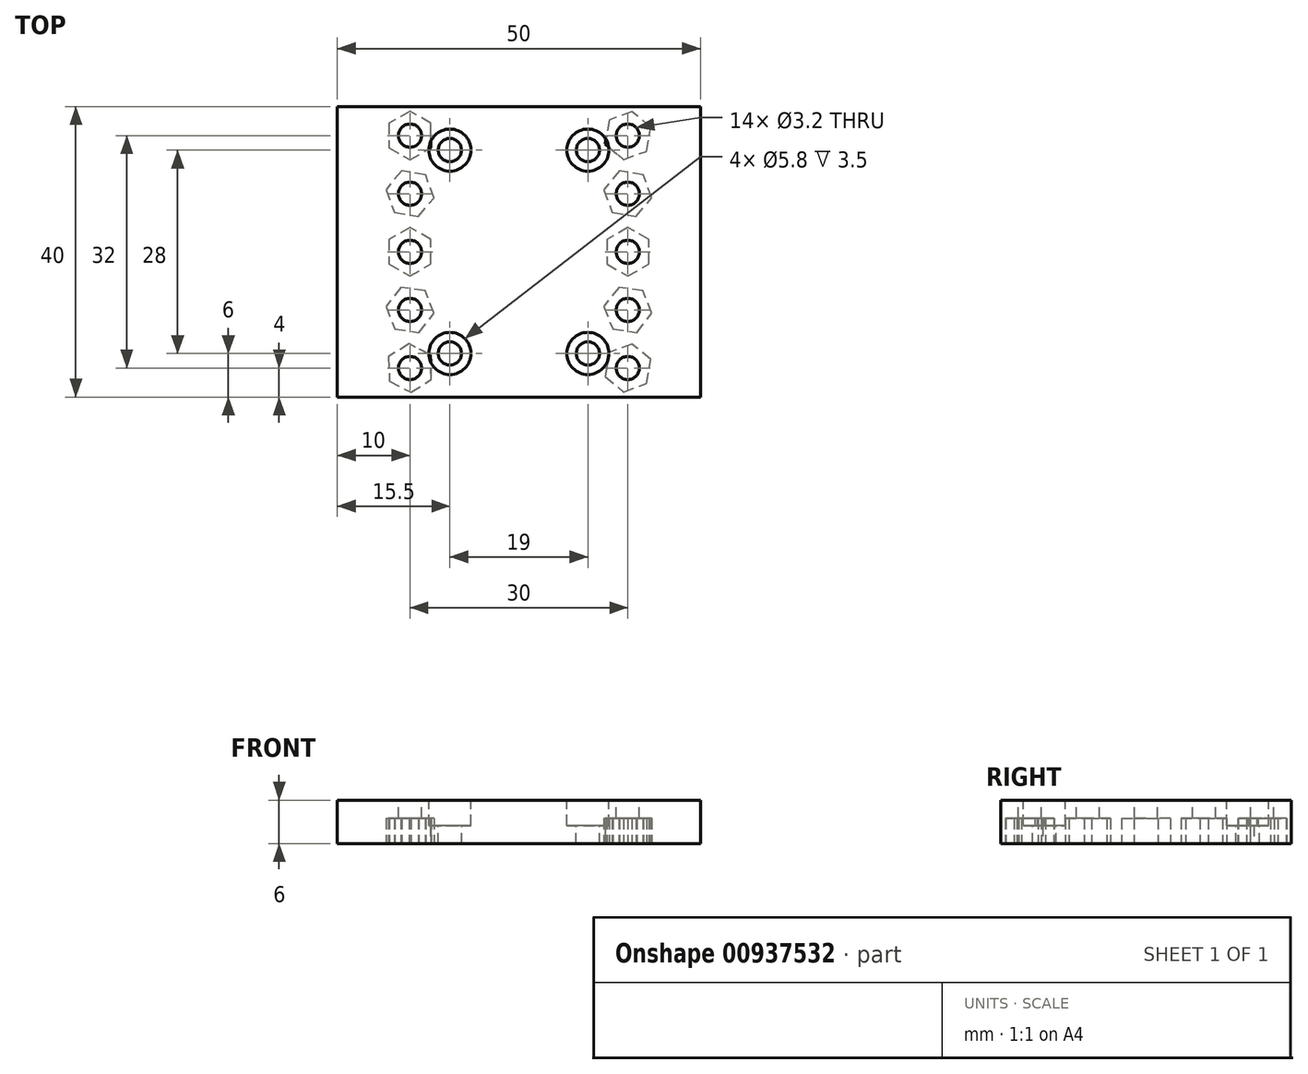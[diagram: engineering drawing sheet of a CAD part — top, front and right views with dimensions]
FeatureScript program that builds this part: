
annotation { "Feature Type Name" : "Feature", "Feature Type Description" : "" }
export const myFeature = defineFeature(function(context is Context, id is Id, definition is map)
    precondition{}
    {
        {
            var Q0;
            Q0=qCreatedBy(makeId("Top.planeOp"),FACE);
            var sketch = newSketch(context, id + "F0", { "sketchPlane" : qUnion([Q0])});
            skLineSegment(sketch, "E0.bottom", {"start": v(25, 20) * mm, "end": v(-25, 20) * mm});
            skLineSegment(sketch, "E0.top", {"start": v(25, -20) * mm, "end": v(-25, -20) * mm});
            skLineSegment(sketch, "E0.left", {"start": v(25, 20) * mm, "end": v(25, -20) * mm});
            skLineSegment(sketch, "E0.right", {"start": v(-25, 20) * mm, "end": v(-25, -20) * mm});
            skPoint(sketch, "E0.middle", {"position": v(0, 0) * mm});
            skSolve(sketch);
        }
        {
            var Q0;
            Q0=makeQuery(id+"F0.imprint","IMPRINT",FACE,{"disambiguationData":[TD([[makeQuery(id+"F0.imprint","IMPRINT",EDGE,{"derivedFrom":sQuery(id+"F0.wireOp",EDGE,"E0.bottom")}),1.0]])]});
            extrude(context, id + "F1", {"entities" : qUnion([Q0]), "depth" : 6 * mm, "offsetDistance" : 25 * mm});
        }
        {
            var Q0;
            Q0=makeQuery(id+"F1.opExtrude","CAP_FACE",FACE,{"disambiguationData":[OSD([sQuery(id+"F0.wireOp",EDGE,"E0.bottom"),sQuery(id+"F0.wireOp",EDGE,"E0.top"),sQuery(id+"F0.wireOp",EDGE,"E0.left"),sQuery(id+"F0.wireOp",EDGE,"E0.right")])],"isStart":false});
            var sketch = newSketch(context, id + "F2", { "sketchPlane" : qUnion([Q0])});
            skCircle(sketch, "E1", {"center": v(-9.5, 14) * mm, "radius": 2.9 * mm});
            skCircle(sketch, "E2.0.1.0", {"center": v(-9.5, -14) * mm, "radius": 2.9 * mm});
            skCircle(sketch, "E2.1.0.0", {"center": v(9.5, 14) * mm, "radius": 2.9 * mm});
            skCircle(sketch, "E2.1.1.0", {"center": v(9.5, -14) * mm, "radius": 2.9 * mm});
            skLineSegment(sketch, "E2.direction1", {"start": v(-9.5, 14) * mm, "end": v(9.5, 14) * mm, "construction": true});
            skLineSegment(sketch, "E2.direction2", {"start": v(-9.5, 14) * mm, "end": v(-9.5, -14) * mm, "construction": true});
            skSolve(sketch);
        }
        {
            var Q0;
            Q0 = qSketchRegion(id + "F2", true);
            extrude(context, id + "F3", {"entities" : qUnion([Q0]), "operationType" : NewBodyOperationType.REMOVE, "oppositeDirection" : true, "depth" : 3.5 * mm, "offsetDistance" : 25 * mm});
        }
        {
            var Q0;
            Q0=makeQuery(id+"F3.boolean.opBoolean","COPY",FACE,{"derivedFrom":makeQuery(id+"F3.opExtrude","CAP_FACE",FACE,{"disambiguationData":[OSD([sQuery(id+"F2.wireOp",EDGE,"E1")])],"isStart":false})});
            var sketch = newSketch(context, id + "F4", { "sketchPlane" : qUnion([Q0])});
            skCircle(sketch, "E3", {"center": v(-9.5, 14) * mm, "radius": 1.6 * mm});
            skCircle(sketch, "E4.0.1.0", {"center": v(-9.5, -14) * mm, "radius": 1.6 * mm});
            skCircle(sketch, "E4.1.0.0", {"center": v(9.5, 14) * mm, "radius": 1.6 * mm});
            skCircle(sketch, "E4.1.1.0", {"center": v(9.5, -14) * mm, "radius": 1.6 * mm});
            skLineSegment(sketch, "E4.direction1", {"start": v(-9.5, 14) * mm, "end": v(9.5, 14) * mm, "construction": true});
            skLineSegment(sketch, "E4.direction2", {"start": v(-9.5, 14) * mm, "end": v(-9.5, -14) * mm, "construction": true});
            skSolve(sketch);
        }
        {
            var Q0;
            Q0 = qSketchRegion(id + "F4", true);
            extrude(context, id + "F5", {"entities" : qUnion([Q0]), "operationType" : NewBodyOperationType.REMOVE, "oppositeDirection" : true, "depth" : 25 * mm, "offsetDistance" : 25 * mm});
        }
        {
            var Q0;
            Q0=makeQuery(id+"F2.imprint","IMPRINT",FACE,{"disambiguationData":[TD([[makeQuery(id+"F2.imprint","IMPRINT",EDGE,{"derivedFrom":sQuery(id+"F2.wireOp",EDGE,"E1")}),-1.0]])]});
            var sketch = newSketch(context, id + "F6", { "sketchPlane" : qUnion([Q0])});
            skCircle(sketch, "E5", {"center": v(-15, 0) * mm, "radius": 1.6 * mm});
            skCircle(sketch, "E6", {"center": v(-15, 8) * mm, "radius": 1.6 * mm});
            skCircle(sketch, "E7", {"center": v(-15, -8) * mm, "radius": 1.6 * mm});
            skCircle(sketch, "E8", {"center": v(15, 0) * mm, "radius": 1.6 * mm});
            skCircle(sketch, "E9", {"center": v(15, 8) * mm, "radius": 1.6 * mm});
            skCircle(sketch, "E10", {"center": v(15, -8) * mm, "radius": 1.6 * mm});
            skCircle(sketch, "E11", {"center": v(-15, -16) * mm, "radius": 1.6 * mm});
            skCircle(sketch, "E12", {"center": v(15, 16) * mm, "radius": 1.6 * mm});
            skCircle(sketch, "E13", {"center": v(-15, 16) * mm, "radius": 1.6 * mm});
            skCircle(sketch, "E14", {"center": v(15, -16) * mm, "radius": 1.6 * mm});
            skSolve(sketch);
        }
        {
            var Q0;
            Q0 = qSketchRegion(id + "F6", true);
            extrude(context, id + "F7", {"entities" : qUnion([Q0]), "operationType" : NewBodyOperationType.REMOVE, "oppositeDirection" : true, "depth" : 25 * mm, "offsetDistance" : 25 * mm});
        }
        {
            var Q0;
            Q0=makeQuery(id+"F1.opExtrude","CAP_FACE",FACE,{"disambiguationData":[OSD([sQuery(id+"F0.wireOp",EDGE,"E0.bottom"),sQuery(id+"F0.wireOp",EDGE,"E0.top"),sQuery(id+"F0.wireOp",EDGE,"E0.left"),sQuery(id+"F0.wireOp",EDGE,"E0.right")])],"isStart":true});
            var sketch = newSketch(context, id + "F8", { "sketchPlane" : qUnion([Q0])});
            skCircle(sketch, "E15.cCircle", {"center": v(-15, 0) * mm, "radius": 2.9 * mm, "construction": true});
            skLineSegment(sketch, "E15.0", {"start": v(-12.1, 1.67) * mm, "end": v(-12.1, -1.67) * mm});
            skLineSegment(sketch, "E15.1", {"start": v(-12.1, -1.67) * mm, "end": v(-15, -3.35) * mm});
            skLineSegment(sketch, "E15.2", {"start": v(-15, -3.35) * mm, "end": v(-17.9, -1.67) * mm});
            skLineSegment(sketch, "E15.3", {"start": v(-17.9, -1.67) * mm, "end": v(-17.9, 1.67) * mm});
            skLineSegment(sketch, "E15.4", {"start": v(-17.9, 1.67) * mm, "end": v(-15, 3.35) * mm});
            skLineSegment(sketch, "E15.5", {"start": v(-15, 3.35) * mm, "end": v(-12.1, 1.67) * mm});
            skPoint(sketch, "E15.0.midPoint", {"position": v(-12.1, 0) * mm});
            skCircle(sketch, "E16.cCircle", {"center": v(-15, 8) * mm, "radius": 2.9 * mm, "construction": true});
            skLineSegment(sketch, "E16.0", {"start": v(-13.76, 11.11) * mm, "end": v(-11.69, 8.49) * mm});
            skLineSegment(sketch, "E16.1", {"start": v(-11.69, 8.49) * mm, "end": v(-12.92, 5.37) * mm});
            skLineSegment(sketch, "E16.2", {"start": v(-12.92, 5.37) * mm, "end": v(-16.24, 4.89) * mm});
            skLineSegment(sketch, "E16.3", {"start": v(-16.24, 4.89) * mm, "end": v(-18.31, 7.51) * mm});
            skLineSegment(sketch, "E16.4", {"start": v(-18.31, 7.51) * mm, "end": v(-17.08, 10.63) * mm});
            skLineSegment(sketch, "E16.5", {"start": v(-17.08, 10.63) * mm, "end": v(-13.76, 11.11) * mm});
            skPoint(sketch, "E16.0.midPoint", {"position": v(-12.73, 9.8) * mm});
            skCircle(sketch, "E17.cCircle", {"center": v(-15, -8) * mm, "radius": 2.9 * mm, "construction": true});
            skLineSegment(sketch, "E17.0", {"start": v(-13.85, -4.86) * mm, "end": v(-11.7, -7.43) * mm});
            skLineSegment(sketch, "E17.1", {"start": v(-11.7, -7.43) * mm, "end": v(-12.85, -10.57) * mm});
            skLineSegment(sketch, "E17.2", {"start": v(-12.85, -10.57) * mm, "end": v(-16.15, -11.14) * mm});
            skLineSegment(sketch, "E17.3", {"start": v(-16.15, -11.14) * mm, "end": v(-18.3, -8.57) * mm});
            skLineSegment(sketch, "E17.4", {"start": v(-18.3, -8.57) * mm, "end": v(-17.15, -5.43) * mm});
            skLineSegment(sketch, "E17.5", {"start": v(-17.15, -5.43) * mm, "end": v(-13.85, -4.86) * mm});
            skPoint(sketch, "E17.0.midPoint", {"position": v(-12.77, -6.14) * mm});
            skCircle(sketch, "E18.cCircle", {"center": v(15, 0) * mm, "radius": 2.9 * mm, "construction": true});
            skLineSegment(sketch, "E18.0", {"start": v(17.9, 1.67) * mm, "end": v(17.9, -1.67) * mm});
            skLineSegment(sketch, "E18.1", {"start": v(17.9, -1.67) * mm, "end": v(15, -3.35) * mm});
            skLineSegment(sketch, "E18.2", {"start": v(15, -3.35) * mm, "end": v(12.1, -1.67) * mm});
            skLineSegment(sketch, "E18.3", {"start": v(12.1, -1.67) * mm, "end": v(12.1, 1.67) * mm});
            skLineSegment(sketch, "E18.4", {"start": v(12.1, 1.67) * mm, "end": v(15, 3.35) * mm});
            skLineSegment(sketch, "E18.5", {"start": v(15, 3.35) * mm, "end": v(17.9, 1.67) * mm});
            skPoint(sketch, "E18.0.midPoint", {"position": v(17.9, 0) * mm});
            skCircle(sketch, "E19.cCircle", {"center": v(15, 8) * mm, "radius": 2.9 * mm, "construction": true});
            skLineSegment(sketch, "E19.0", {"start": v(16.24, 11.11) * mm, "end": v(18.31, 8.49) * mm});
            skLineSegment(sketch, "E19.1", {"start": v(18.31, 8.49) * mm, "end": v(17.08, 5.37) * mm});
            skLineSegment(sketch, "E19.2", {"start": v(17.08, 5.37) * mm, "end": v(13.76, 4.89) * mm});
            skLineSegment(sketch, "E19.3", {"start": v(13.76, 4.89) * mm, "end": v(11.69, 7.51) * mm});
            skLineSegment(sketch, "E19.4", {"start": v(11.69, 7.51) * mm, "end": v(12.92, 10.63) * mm});
            skLineSegment(sketch, "E19.5", {"start": v(12.92, 10.63) * mm, "end": v(16.24, 11.11) * mm});
            skPoint(sketch, "E19.0.midPoint", {"position": v(17.27, 9.8) * mm});
            skCircle(sketch, "E20.cCircle", {"center": v(15, -8) * mm, "radius": 2.9 * mm, "construction": true});
            skLineSegment(sketch, "E20.0", {"start": v(16.15, -4.86) * mm, "end": v(18.3, -7.43) * mm});
            skLineSegment(sketch, "E20.1", {"start": v(18.3, -7.43) * mm, "end": v(17.15, -10.57) * mm});
            skLineSegment(sketch, "E20.2", {"start": v(17.15, -10.57) * mm, "end": v(13.85, -11.14) * mm});
            skLineSegment(sketch, "E20.3", {"start": v(13.85, -11.14) * mm, "end": v(11.7, -8.57) * mm});
            skLineSegment(sketch, "E20.4", {"start": v(11.7, -8.57) * mm, "end": v(12.85, -5.43) * mm});
            skLineSegment(sketch, "E20.5", {"start": v(12.85, -5.43) * mm, "end": v(16.15, -4.86) * mm});
            skPoint(sketch, "E20.0.midPoint", {"position": v(17.23, -6.14) * mm});
            skCircle(sketch, "E21.cCircle", {"center": v(-15, 16) * mm, "radius": 2.9 * mm, "construction": true});
            skLineSegment(sketch, "E21.0", {"start": v(-14.86, 19.35) * mm, "end": v(-12.03, 17.56) * mm});
            skLineSegment(sketch, "E21.1", {"start": v(-12.03, 17.56) * mm, "end": v(-12.17, 14.2) * mm});
            skLineSegment(sketch, "E21.2", {"start": v(-12.17, 14.2) * mm, "end": v(-15.14, 12.65) * mm});
            skLineSegment(sketch, "E21.3", {"start": v(-15.14, 12.65) * mm, "end": v(-17.97, 14.44) * mm});
            skLineSegment(sketch, "E21.4", {"start": v(-17.97, 14.44) * mm, "end": v(-17.83, 17.8) * mm});
            skLineSegment(sketch, "E21.5", {"start": v(-17.83, 17.8) * mm, "end": v(-14.86, 19.35) * mm});
            skPoint(sketch, "E21.0.midPoint", {"position": v(-13.45, 18.45) * mm});
            skCircle(sketch, "E22.cCircle", {"center": v(-15, -16) * mm, "radius": 2.9 * mm, "construction": true});
            skLineSegment(sketch, "E22.0", {"start": v(-17.9, -17.67) * mm, "end": v(-17.9, -14.33) * mm});
            skLineSegment(sketch, "E22.1", {"start": v(-17.9, -14.33) * mm, "end": v(-15, -12.65) * mm});
            skLineSegment(sketch, "E22.2", {"start": v(-15, -12.65) * mm, "end": v(-12.1, -14.33) * mm});
            skLineSegment(sketch, "E22.3", {"start": v(-12.1, -14.33) * mm, "end": v(-12.1, -17.67) * mm});
            skLineSegment(sketch, "E22.4", {"start": v(-12.1, -17.67) * mm, "end": v(-15, -19.35) * mm});
            skLineSegment(sketch, "E22.5", {"start": v(-15, -19.35) * mm, "end": v(-17.9, -17.67) * mm});
            skPoint(sketch, "E22.0.midPoint", {"position": v(-17.9, -16) * mm});
            skCircle(sketch, "E23.cCircle", {"center": v(15, 16) * mm, "radius": 2.9 * mm, "construction": true});
            skLineSegment(sketch, "E23.0", {"start": v(17.57, 18.15) * mm, "end": v(18.14, 14.85) * mm});
            skLineSegment(sketch, "E23.1", {"start": v(18.14, 14.85) * mm, "end": v(15.57, 12.7) * mm});
            skLineSegment(sketch, "E23.2", {"start": v(15.57, 12.7) * mm, "end": v(12.43, 13.85) * mm});
            skLineSegment(sketch, "E23.3", {"start": v(12.43, 13.85) * mm, "end": v(11.86, 17.15) * mm});
            skLineSegment(sketch, "E23.4", {"start": v(11.86, 17.15) * mm, "end": v(14.43, 19.3) * mm});
            skLineSegment(sketch, "E23.5", {"start": v(14.43, 19.3) * mm, "end": v(17.57, 18.15) * mm});
            skPoint(sketch, "E23.0.midPoint", {"position": v(17.86, 16.5) * mm});
            skCircle(sketch, "E24.cCircle", {"center": v(15, -16) * mm, "radius": 2.9 * mm, "construction": true});
            skLineSegment(sketch, "E24.0", {"start": v(17.57, -13.85) * mm, "end": v(18.14, -17.15) * mm});
            skLineSegment(sketch, "E24.1", {"start": v(18.14, -17.15) * mm, "end": v(15.57, -19.3) * mm});
            skLineSegment(sketch, "E24.2", {"start": v(15.57, -19.3) * mm, "end": v(12.43, -18.15) * mm});
            skLineSegment(sketch, "E24.3", {"start": v(12.43, -18.15) * mm, "end": v(11.86, -14.85) * mm});
            skLineSegment(sketch, "E24.4", {"start": v(11.86, -14.85) * mm, "end": v(14.43, -12.7) * mm});
            skLineSegment(sketch, "E24.5", {"start": v(14.43, -12.7) * mm, "end": v(17.57, -13.85) * mm});
            skPoint(sketch, "E24.0.midPoint", {"position": v(17.86, -15.5) * mm});
            skSolve(sketch);
        }
        {
            var Q0;
            Q0 = qSketchRegion(id + "F8", true);
            extrude(context, id + "F9", {"entities" : qUnion([Q0]), "operationType" : NewBodyOperationType.REMOVE, "oppositeDirection" : true, "depth" : 3.5 * mm, "offsetDistance" : 25 * mm});
        }
    });
